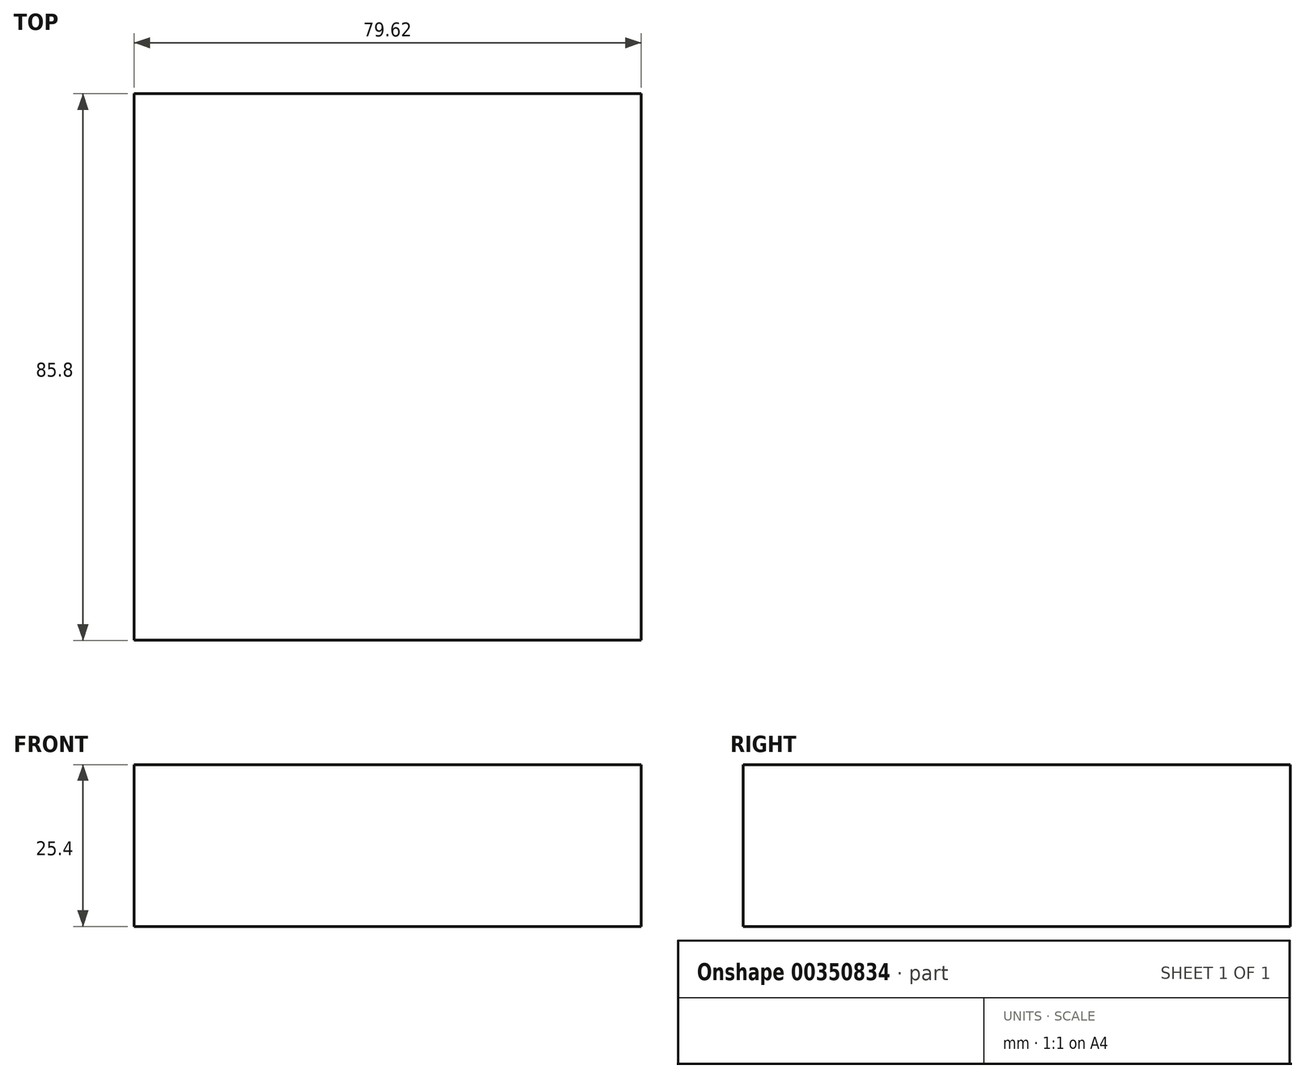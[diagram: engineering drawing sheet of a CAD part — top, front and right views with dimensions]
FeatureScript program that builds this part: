
annotation { "Feature Type Name" : "Feature", "Feature Type Description" : "" }
export const myFeature = defineFeature(function(context is Context, id is Id, definition is map)
    precondition{}
    {
        {
            var Q0;
            Q0=qCreatedBy(makeId("Top.planeOp"),FACE);
            var sketch = newSketch(context, id + "F0", { "sketchPlane" : qUnion([Q0])});
            skLineSegment(sketch, "E0.bottom", {"start": v(-39.9, 47.12) * mm, "end": v(39.72, 47.12) * mm});
            skLineSegment(sketch, "E0.top", {"start": v(-39.9, -38.68) * mm, "end": v(39.72, -38.68) * mm});
            skLineSegment(sketch, "E0.left", {"start": v(-39.9, 47.12) * mm, "end": v(-39.9, -38.68) * mm});
            skLineSegment(sketch, "E0.right", {"start": v(39.72, 47.12) * mm, "end": v(39.72, -38.68) * mm});
            skLineSegment(sketch, "E1.bottom", {"start": v(39.72, 0) * mm, "end": v(39.72, 0) * mm});
            skLineSegment(sketch, "E1.top", {"start": v(39.72, 0) * mm, "end": v(39.72, 0) * mm});
            skLineSegment(sketch, "E1.left", {"start": v(39.72, 0) * mm, "end": v(39.72, 0) * mm});
            skLineSegment(sketch, "E1.right", {"start": v(39.72, 0) * mm, "end": v(39.72, 0) * mm});
            skSolve(sketch);
        }
        {
            var Q0;
            Q0=makeQuery(id+"F0.imprint","IMPRINT",FACE,{"disambiguationData":[TD([[makeQuery(id+"F0.imprint","IMPRINT",EDGE,{"derivedFrom":sQuery(id+"F0.wireOp",EDGE,"E0.bottom")}),-1.0]])]});
            var Q1;
            Q1=sQuery(id+"F0.wireOp",EDGE,"E0.right");
            var Q2;
            Q2=sQuery(id+"F0.wireOp",EDGE,"E0.bottom");
            var Q3;
            Q3=sQuery(id+"F0.wireOp",EDGE,"E0.left");
            var Q4;
            Q4=sQuery(id+"F0.wireOp",EDGE,"E0.top");
            extrude(context, id + "F1", {"entities" : qUnion([Q0]), "surfaceEntities" : qUnion([Q1, Q2, Q3, Q4]), "depth" : 25.4 * mm});
        }
    });
